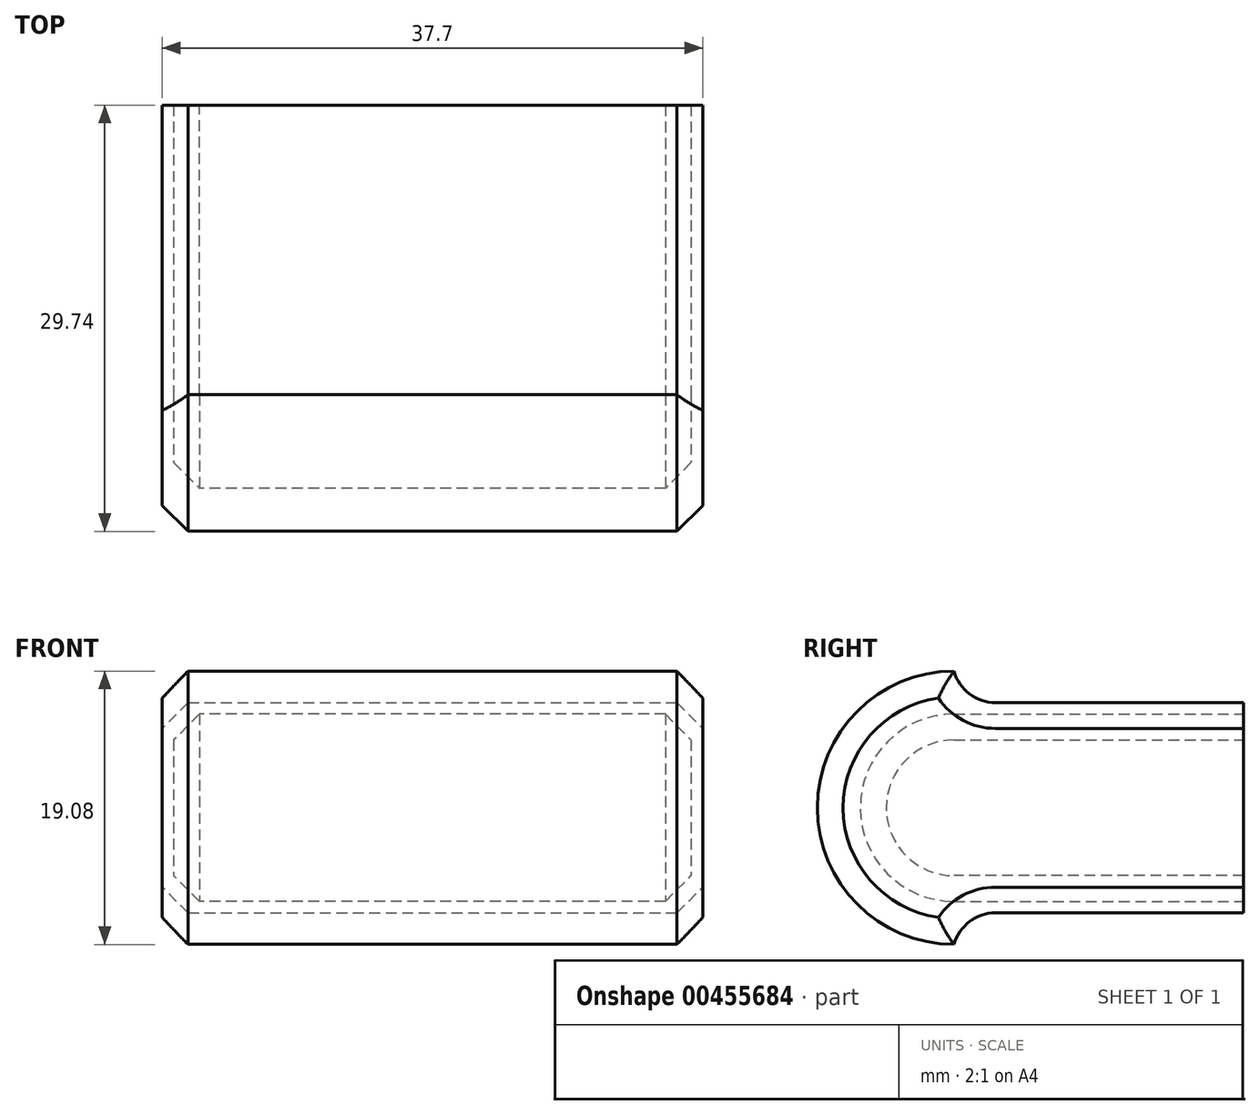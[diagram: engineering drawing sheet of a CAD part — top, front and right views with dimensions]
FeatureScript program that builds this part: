
annotation { "Feature Type Name" : "Feature", "Feature Type Description" : "" }
export const myFeature = defineFeature(function(context is Context, id is Id, definition is map)
    precondition{}
    {
        {
            assignVariable(context, id + "F0", {"name" : "clearance", "anyValue" : 0.2});
        }
        {
            assignVariable(context, id + "F1", {"name" : "shell_thickness", "anyValue" : 0.8});
        }
        {
            assignVariable(context, id + "F2", {"name" : "dome_thickness", "anyValue" : 3});
        }
        {
            var Q0;
            Q0=qCreatedBy(makeId("Right.planeOp"),FACE);
            var sketch = newSketch(context, id + "F3", { "sketchPlane" : qUnion([Q0])});
            skLineSegment(sketch, "E0.bottom", {"start": v(0, 6.54) * mm, "end": v(20.2, 6.54) * mm});
            skLineSegment(sketch, "E0.top", {"start": v(0, -6.54) * mm, "end": v(20.2, -6.54) * mm});
            skLineSegment(sketch, "E0.left", {"start": v(0, 7.34) * mm, "end": v(0, -6.94) * mm, "construction": true});
            skLineSegment(sketch, "E0.right", {"start": v(20.2, 7.34) * mm, "end": v(20.2, -7.34) * mm});
            skArc(sketch, "E1", {"start": v(0, 6.54) * mm, "mid": v(-6.54, 0) * mm, "end": v(0, -6.54) * mm});
            skLineSegment(sketch, "E2.0", {"start": v(0, 7.34) * mm, "end": v(20.2, 7.34) * mm});
            skArc(sketch, "E3.0", {"start": v(0, 9.54) * mm, "mid": v(-9.54, 0) * mm, "end": v(0, -9.54) * mm});
            skLineSegment(sketch, "E4", {"start": v(0, 9.54) * mm, "end": v(0, 7.34) * mm});
            skLineSegment(sketch, "E5", {"start": v(0, -9.54) * mm, "end": v(0, -6.94) * mm});
            skLineSegment(sketch, "E6.0", {"start": v(0, -7.34) * mm, "end": v(20.2, -7.34) * mm});
            skSolve(sketch);
        }
        {
            var Q0;
            Q0=makeQuery(id+"F3.imprint","IMPRINT",FACE,{"disambiguationData":[TD([[makeQuery(id+"F3.imprint","IMPRINT",EDGE,{"derivedFrom":sQuery(id+"F3.wireOp",EDGE,"E0.bottom")}),-1.0]])]});
            var Q1;
            Q1=makeQuery(id+"F3.imprint","IMPRINT",FACE,{"disambiguationData":[TD([[makeQuery(id+"F3.imprint","IMPRINT",EDGE,{"derivedFrom":sQuery(id+"F3.wireOp",EDGE,"E0.bottom")}),1.0]])]});
            extrude(context, id + "F4", {"entities" : qUnion([Q0, Q1]), "oppositeDirection" : true, "depth" : (getVariable(context, 'shell_thickness')) * mm, "hasSecondDirection" : true, "secondDirectionOppositeDirection" : false, "secondDirectionDepth" : (35.9 + getVariable(context, 'clearance') + getVariable(context, 'shell_thickness')) * mm});
        }
        {
            var Q0;
            {var subQ0=sQuery(id+"F3.wireOp",EDGE,"E0.bottom");Q0=makeQuery(id+"F3.imprint","IMPRINT",FACE,{"disambiguationData":[TD([[makeQuery(id+"F3.imprint","IMPRINT",EDGE,{"derivedFrom":subQ0}),-1.0]])]});}
            extrude(context, id + "F5", {"entities" : qUnion([Q0]), "operationType" : NewBodyOperationType.REMOVE, "depth" : (35.9 + getVariable(context, 'clearance')) * mm});
        }
        {
            var Q0;
            Q0=makeQuery(id+"F4.opExtrude","SWEPT_EDGE",EDGE,{"disambiguationData":[OSD([sQuery(id+"F3.wireOp",EDGE,"E2.0"),sQuery(id+"F3.wireOp",EDGE,"E4")])]});
            var Q1;
            Q1=makeQuery(id+"F4.opExtrude","SWEPT_EDGE",EDGE,{"disambiguationData":[OSD([sQuery(id+"F3.wireOp",EDGE,"E5"),sQuery(id+"F3.wireOp",EDGE,"E6.0")])]});
            fillet(context, id + "F6", {"entities" : qUnion([Q0, Q1]), "radius" : (getVariable(context, 'dome_thickness')) * mm, "tangentPropagation" : true, "allowEdgeOverflow" : false});
        }
        {
            var Q0;
            Q0=makeQuery(id+"F5.boolean.opBoolean","COPY",EDGE,{"derivedFrom":makeQuery(id+"F5.opExtrude","CAP_EDGE",EDGE,{"disambiguationData":[OSD([sQuery(id+"F3.wireOp",EDGE,"E0.bottom")])],"isStart":false})});
            var Q1;
            Q1=makeQuery(id+"F5.boolean.opBoolean","COPY",EDGE,{"derivedFrom":makeQuery(id+"F5.opExtrude","CAP_EDGE",EDGE,{"disambiguationData":[OSD([sQuery(id+"F3.wireOp",EDGE,"E1")])],"isStart":true})});
            chamfer(context, id + "F7", {"entities" : qUnion([Q0, Q1]), "width" : 1.8 * mm, "tangentPropagation" : true});
        }
        {
            var Q0;
            Q0=makeQuery(id+"F4.opExtrude","CAP_EDGE",EDGE,{"disambiguationData":[OSD([sQuery(id+"F3.wireOp",EDGE,"E2.0")])],"isStart":true});
            var Q1;
            {var subQ0=sQuery(id+"F3.wireOp",EDGE,"E4");var subQ1=sQuery(id+"F3.wireOp",EDGE,"E2.0");Q1=makeQuery(id+"F6.opFillet","BLEND_EDGE",EDGE,{"blendedFrom":[makeQuery(id+"F4.opExtrude","SWEPT_EDGE",EDGE,{"disambiguationData":[OSD([subQ1,subQ0])]}),makeQuery(id+"F4.opExtrude","CAP_FACE",FACE,{"disambiguationData":[OSD([sQuery(id+"F3.wireOp",EDGE,"E0.right"),subQ1,sQuery(id+"F3.wireOp",EDGE,"E3.0"),subQ0,sQuery(id+"F3.wireOp",EDGE,"E5"),sQuery(id+"F3.wireOp",EDGE,"E6.0")])],"isStart":true})],"blendedInto":[makeQuery(id+"F4.opExtrude","CAP_FACE",FACE,{"disambiguationData":[OSD([sQuery(id+"F3.wireOp",EDGE,"E0.right"),subQ1,sQuery(id+"F3.wireOp",EDGE,"E3.0"),subQ0,sQuery(id+"F3.wireOp",EDGE,"E5"),sQuery(id+"F3.wireOp",EDGE,"E6.0")])],"isStart":true})]});}
            var Q2;
            Q2=makeQuery(id+"F4.opExtrude","CAP_EDGE",EDGE,{"disambiguationData":[OSD([sQuery(id+"F3.wireOp",EDGE,"E3.0")])],"isStart":true});
            var Q3;
            {var subQ0=sQuery(id+"F3.wireOp",EDGE,"E6.0");var subQ1=sQuery(id+"F3.wireOp",EDGE,"E5");Q3=makeQuery(id+"F6.opFillet","BLEND_EDGE",EDGE,{"blendedFrom":[makeQuery(id+"F4.opExtrude","SWEPT_EDGE",EDGE,{"disambiguationData":[OSD([subQ1,subQ0])]}),makeQuery(id+"F4.opExtrude","CAP_FACE",FACE,{"disambiguationData":[OSD([sQuery(id+"F3.wireOp",EDGE,"E0.right"),sQuery(id+"F3.wireOp",EDGE,"E2.0"),sQuery(id+"F3.wireOp",EDGE,"E3.0"),sQuery(id+"F3.wireOp",EDGE,"E4"),subQ1,subQ0])],"isStart":true})],"blendedInto":[makeQuery(id+"F4.opExtrude","CAP_FACE",FACE,{"disambiguationData":[OSD([sQuery(id+"F3.wireOp",EDGE,"E0.right"),sQuery(id+"F3.wireOp",EDGE,"E2.0"),sQuery(id+"F3.wireOp",EDGE,"E3.0"),sQuery(id+"F3.wireOp",EDGE,"E4"),subQ1,subQ0])],"isStart":true})]});}
            var Q4;
            Q4=makeQuery(id+"F4.opExtrude","CAP_EDGE",EDGE,{"disambiguationData":[OSD([sQuery(id+"F3.wireOp",EDGE,"E6.0")])],"isStart":true});
            var Q5;
            Q5=makeQuery(id+"F4.opExtrude","CAP_EDGE",EDGE,{"disambiguationData":[OSD([sQuery(id+"F3.wireOp",EDGE,"E2.0")])],"isStart":false});
            var Q6;
            {var subQ0=sQuery(id+"F3.wireOp",EDGE,"E4");var subQ1=sQuery(id+"F3.wireOp",EDGE,"E2.0");Q6=makeQuery(id+"F6.opFillet","BLEND_EDGE",EDGE,{"blendedFrom":[makeQuery(id+"F4.opExtrude","SWEPT_EDGE",EDGE,{"disambiguationData":[OSD([subQ1,subQ0])]}),makeQuery(id+"F4.opExtrude","CAP_FACE",FACE,{"disambiguationData":[OSD([sQuery(id+"F3.wireOp",EDGE,"E0.right"),subQ1,sQuery(id+"F3.wireOp",EDGE,"E3.0"),subQ0,sQuery(id+"F3.wireOp",EDGE,"E5"),sQuery(id+"F3.wireOp",EDGE,"E6.0")])],"isStart":false})],"blendedInto":[makeQuery(id+"F4.opExtrude","CAP_FACE",FACE,{"disambiguationData":[OSD([sQuery(id+"F3.wireOp",EDGE,"E0.right"),subQ1,sQuery(id+"F3.wireOp",EDGE,"E3.0"),subQ0,sQuery(id+"F3.wireOp",EDGE,"E5"),sQuery(id+"F3.wireOp",EDGE,"E6.0")])],"isStart":false})]});}
            var Q7;
            Q7=makeQuery(id+"F4.opExtrude","CAP_EDGE",EDGE,{"disambiguationData":[OSD([sQuery(id+"F3.wireOp",EDGE,"E3.0")])],"isStart":false});
            var Q8;
            {var subQ0=sQuery(id+"F3.wireOp",EDGE,"E6.0");var subQ1=sQuery(id+"F3.wireOp",EDGE,"E5");Q8=makeQuery(id+"F6.opFillet","BLEND_EDGE",EDGE,{"blendedFrom":[makeQuery(id+"F4.opExtrude","SWEPT_EDGE",EDGE,{"disambiguationData":[OSD([subQ1,subQ0])]}),makeQuery(id+"F4.opExtrude","CAP_FACE",FACE,{"disambiguationData":[OSD([sQuery(id+"F3.wireOp",EDGE,"E0.right"),sQuery(id+"F3.wireOp",EDGE,"E2.0"),sQuery(id+"F3.wireOp",EDGE,"E3.0"),sQuery(id+"F3.wireOp",EDGE,"E4"),subQ1,subQ0])],"isStart":false})],"blendedInto":[makeQuery(id+"F4.opExtrude","CAP_FACE",FACE,{"disambiguationData":[OSD([sQuery(id+"F3.wireOp",EDGE,"E0.right"),sQuery(id+"F3.wireOp",EDGE,"E2.0"),sQuery(id+"F3.wireOp",EDGE,"E3.0"),sQuery(id+"F3.wireOp",EDGE,"E4"),subQ1,subQ0])],"isStart":false})]});}
            var Q9;
            Q9=makeQuery(id+"F4.opExtrude","CAP_EDGE",EDGE,{"disambiguationData":[OSD([sQuery(id+"F3.wireOp",EDGE,"E6.0")])],"isStart":false});
            chamfer(context, id + "F8", {"entities" : qUnion([Q0, Q1, Q2, Q3, Q4, Q5, Q6, Q7, Q8, Q9]), "width" : 1.8 * mm});
        }
    });
